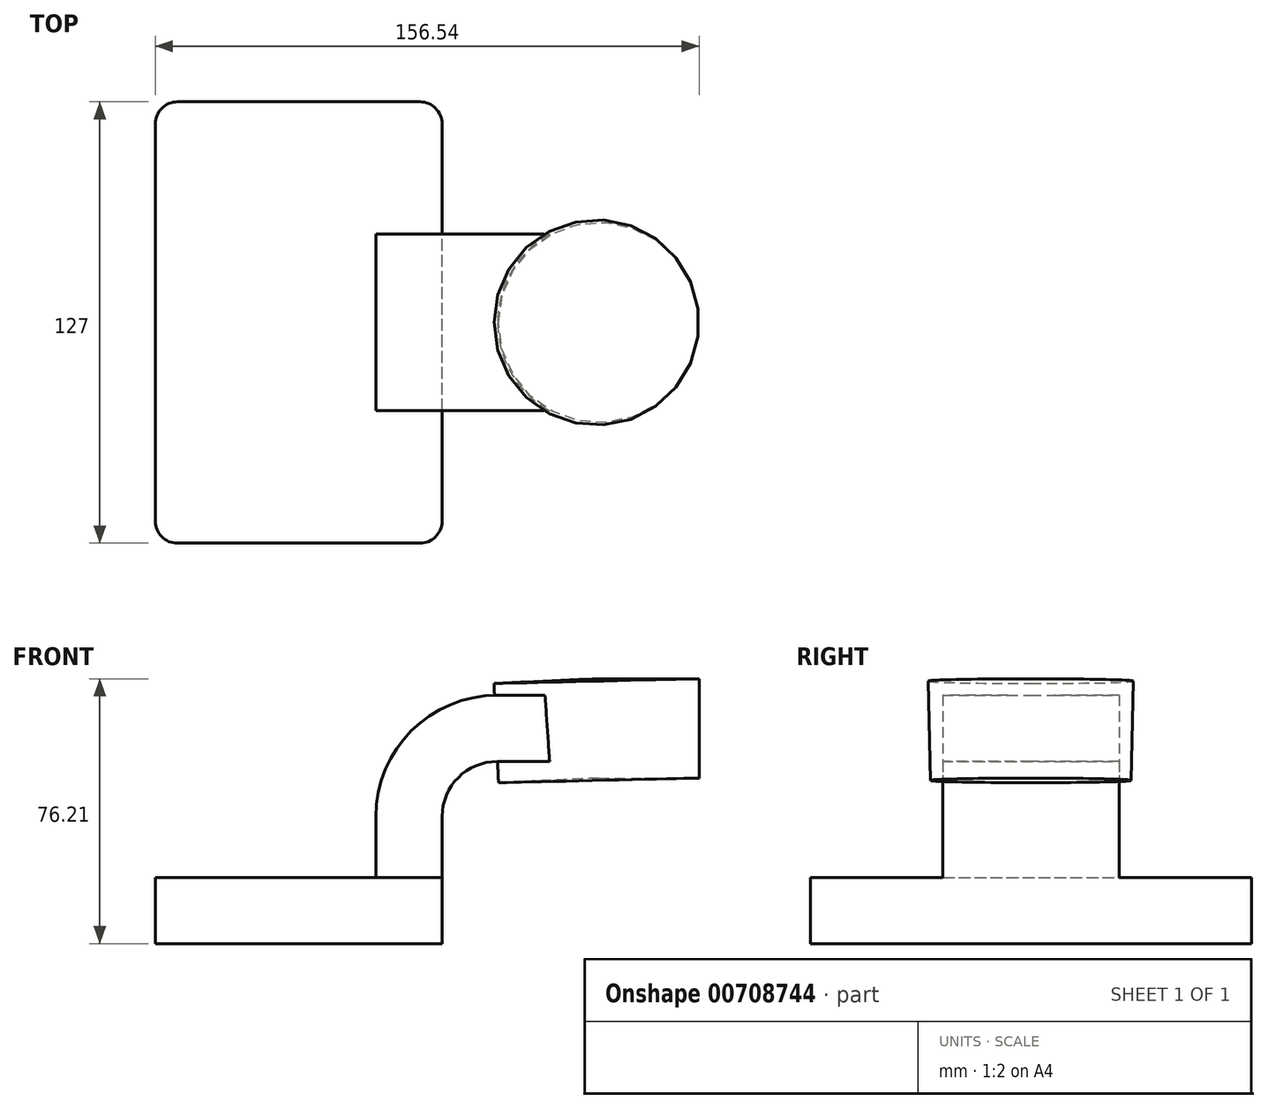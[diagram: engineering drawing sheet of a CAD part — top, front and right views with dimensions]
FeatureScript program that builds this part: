
annotation { "Feature Type Name" : "Feature", "Feature Type Description" : "" }
export const myFeature = defineFeature(function(context is Context, id is Id, definition is map)
    precondition{}
    {
        {
            var Q0;
            Q0=qCreatedBy(makeId("Front.planeOp"),FACE);
            var sketch = newSketch(context, id + "F0", { "sketchPlane" : qUnion([Q0])});
            skLineSegment(sketch, "E0.bottom", {"start": v(-41.28, 9.52) * mm, "end": v(41.27, 9.53) * mm});
            skLineSegment(sketch, "E0.top", {"start": v(-41.28, -9.53) * mm, "end": v(41.28, -9.53) * mm});
            skLineSegment(sketch, "E0.left", {"start": v(-41.28, 9.52) * mm, "end": v(-41.27, -9.53) * mm});
            skLineSegment(sketch, "E0.right", {"start": v(41.28, 9.53) * mm, "end": v(41.28, -9.52) * mm});
            skPoint(sketch, "E0.middle", {"position": v(0, 0) * mm});
            skLineSegment(sketch, "E1.bottom", {"start": v(64.47, 38.1) * mm, "end": v(115.27, 38.1) * mm});
            skLineSegment(sketch, "E1.top", {"start": v(64.47, 66.67) * mm, "end": v(115.27, 66.67) * mm});
            skLineSegment(sketch, "E1.left", {"start": v(64.47, 38.1) * mm, "end": v(64.47, 66.67) * mm});
            skLineSegment(sketch, "E1.right", {"start": v(115.27, 38.1) * mm, "end": v(115.27, 66.67) * mm});
            skPoint(sketch, "E1.middle", {"position": v(89.87, 52.39) * mm});
            skLineSegment(sketch, "E2", {"start": v(41.27, 9.53) * mm, "end": v(41.27, 27) * mm});
            skArc(sketch, "E3", {"start": v(41.27, 27) * mm, "mid": v(45.92, 38.23) * mm, "end": v(57.15, 42.88) * mm});
            skLineSegment(sketch, "E4", {"start": v(57.15, 42.88) * mm, "end": v(85.73, 42.88) * mm});
            skLineSegment(sketch, "E5.0", {"start": v(57.15, 61.93) * mm, "end": v(85.73, 61.93) * mm});
            skArc(sketch, "E5.1", {"start": v(22.22, 27) * mm, "mid": v(32.45, 51.7) * mm, "end": v(57.15, 61.93) * mm});
            skLineSegment(sketch, "E5.2", {"start": v(22.22, 9.53) * mm, "end": v(22.22, 27) * mm});
            skFitSpline(sketch, "E6", {"points": [v(64.47, 61.93) * mm, v(-41.28, 9.52) * mm], "startDerivative": vector(-122.69, 22.07) * mm, "endDerivative": vector(-1.24, -83.87) * mm});
            skFitSpline(sketch, "E7", {"points": [v(-213.67, 37.06) * mm, v(-214.09, 37.06) * mm], "startDerivative": vector(-0.42, 0) * mm, "endDerivative": vector(-0.42, 0) * mm});
            skLineSegment(sketch, "E8", {"start": v(85.73, 42.88) * mm, "end": v(85.73, 61.93) * mm});
            skLineSegment(sketch, "E9", {"start": v(86.38, 38.1) * mm, "end": v(85.72, 66.67) * mm});
            skSolve(sketch);
        }
        {
            var Q0;
            Q0=makeQuery(id+"F0.imprint","IMPRINT",FACE,{"disambiguationData":[TD([[makeQuery(id+"F0.imprint","IMPRINT",EDGE,{"derivedFrom":sQuery(id+"F0.wireOp",EDGE,"E0.top")}),1.0]])]});
            extrude(context, id + "F1", {"entities" : qUnion([Q0]), "endBound" : BoundingType.SYMMETRIC, "depth" : 127 * mm, "offsetDistance" : 25.4 * mm});
        }
        {
            var Q0;
            {var subQ5=sQuery(id+"F0.wireOp",EDGE,"E8");Q0=makeQuery(id+"F0.imprint","IMPRINT",FACE,{"disambiguationData":[TD([[makeQuery(id+"F0.imprint","IMPRINT",EDGE,{"derivedFrom":subQ5}),1.0]])]});}
            var Q1;
            {var subQ1=sQuery(id+"F0.wireOp",EDGE,"E2");Q1=makeQuery(id+"F0.imprint","IMPRINT",FACE,{"disambiguationData":[TD([[makeQuery(id+"F0.imprint","IMPRINT",EDGE,{"derivedFrom":subQ1}),1.0]])]});}
            extrude(context, id + "F2", {"entities" : qUnion([Q0, Q1]), "operationType" : NewBodyOperationType.ADD, "endBound" : BoundingType.SYMMETRIC, "depth" : 50.8 * mm, "offsetDistance" : 25.4 * mm});
        }
        {
            var Q0;
            {var subQ1=sQuery(id+"F0.wireOp",EDGE,"E5.1");Q0=makeQuery(id+"F0.imprint","IMPRINT",FACE,{"disambiguationData":[TD([[makeQuery(id+"F0.imprint","IMPRINT",EDGE,{"derivedFrom":subQ1}),1.0]])]});}
            extrude(context, id + "F3", {"entities" : qUnion([Q0]), "operationType" : NewBodyOperationType.ADD, "endBound" : BoundingType.SYMMETRIC, "depth" : 15.88 * mm, "offsetDistance" : 25.4 * mm});
        }
        {
            var Q0;
            {var subQ0=sQuery(id+"F0.wireOp",EDGE,"E1.right");Q0=makeQuery(id+"F0.imprint","IMPRINT",FACE,{"disambiguationData":[TD([[makeQuery(id+"F0.imprint","IMPRINT",EDGE,{"derivedFrom":subQ0}),1.0]])]});}
            var Q1;
            Q1=sQuery(id+"F0.wireOp",EDGE,"E9");
            revolve(context, id + "F4", {"operationType" : NewBodyOperationType.ADD, "entities" : qUnion([Q0]), "axis" : qUnion([Q1]), "revolveType" : RevolveType.FULL});
        }
        {
            var Q0;
            Q0=makeQuery(id+"F1.opExtrude","CAP_EDGE",EDGE,{"disambiguationData":[OSD([sQuery(id+"F0.wireOp",EDGE,"E0.left")])],"isStart":false});
            var Q1;
            Q1=makeQuery(id+"F1.opExtrude","CAP_EDGE",EDGE,{"disambiguationData":[OSD([sQuery(id+"F0.wireOp",EDGE,"E0.right")])],"isStart":false});
            var Q2;
            Q2=makeQuery(id+"F1.opExtrude","CAP_EDGE",EDGE,{"disambiguationData":[OSD([sQuery(id+"F0.wireOp",EDGE,"E0.right")])],"isStart":true});
            var Q3;
            Q3=makeQuery(id+"F1.opExtrude","CAP_EDGE",EDGE,{"disambiguationData":[OSD([sQuery(id+"F0.wireOp",EDGE,"E0.left")])],"isStart":true});
            fillet(context, id + "F5", {"entities" : qUnion([Q0, Q1, Q2, Q3]), "radius" : 6.35 * mm, "tangentPropagation" : true, "allowEdgeOverflow" : false});
        }
    });
